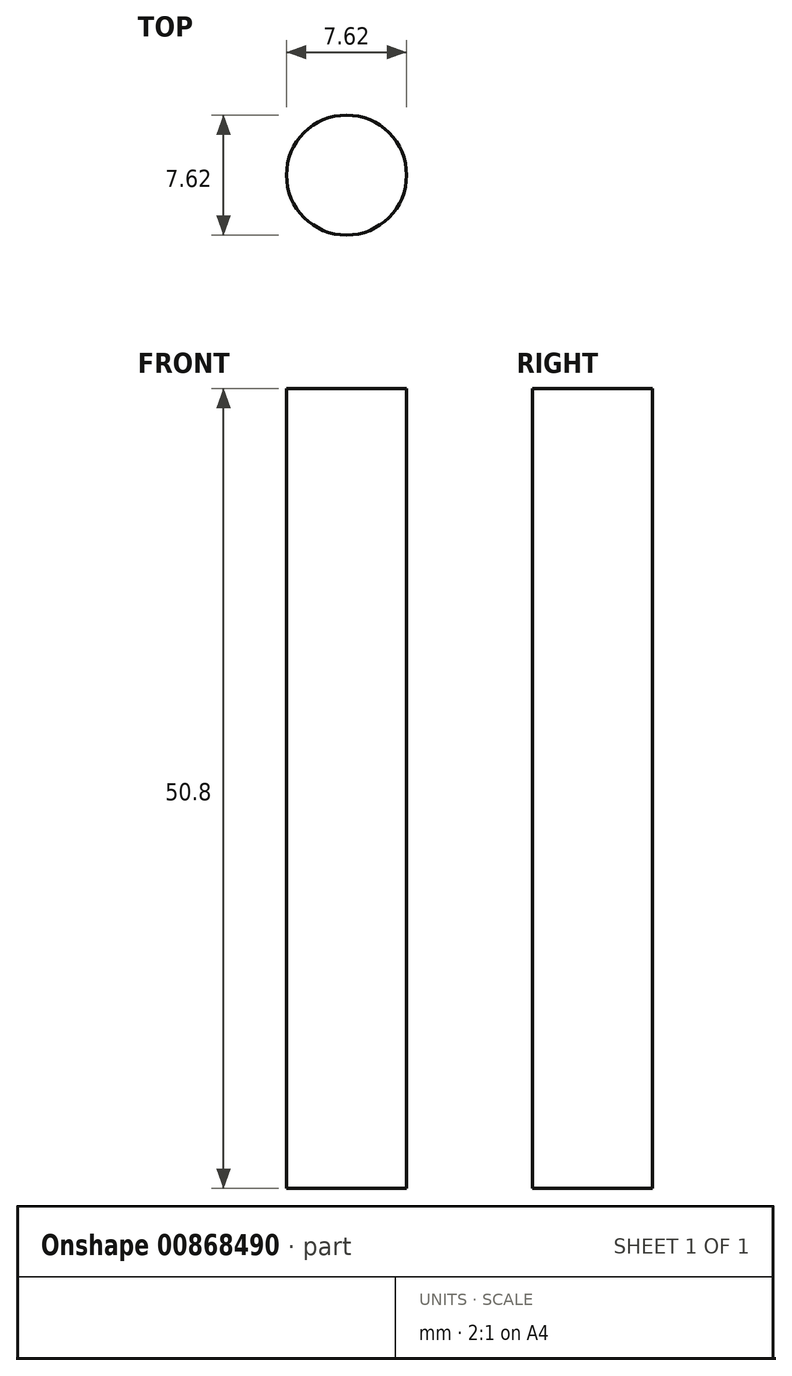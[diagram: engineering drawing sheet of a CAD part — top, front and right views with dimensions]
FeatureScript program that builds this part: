
annotation { "Feature Type Name" : "Feature", "Feature Type Description" : "" }
export const myFeature = defineFeature(function(context is Context, id is Id, definition is map)
    precondition{}
    {
        {
            var Q0;
            Q0=qCreatedBy(makeId("Top.planeOp"),FACE);
            var sketch = newSketch(context, id + "F0", { "sketchPlane" : qUnion([Q0])});
            skCircle(sketch, "E0", {"center": v(0, 0) * mm, "radius": 3.81 * mm});
            skSolve(sketch);
        }
        {
            var Q0;
            Q0 = qSketchRegion(id + "F0", true);
            extrude(context, id + "F1", {"entities" : qUnion([Q0]), "depth" : 50.8 * mm, "offsetDistance" : 25.4 * mm});
        }
    });
